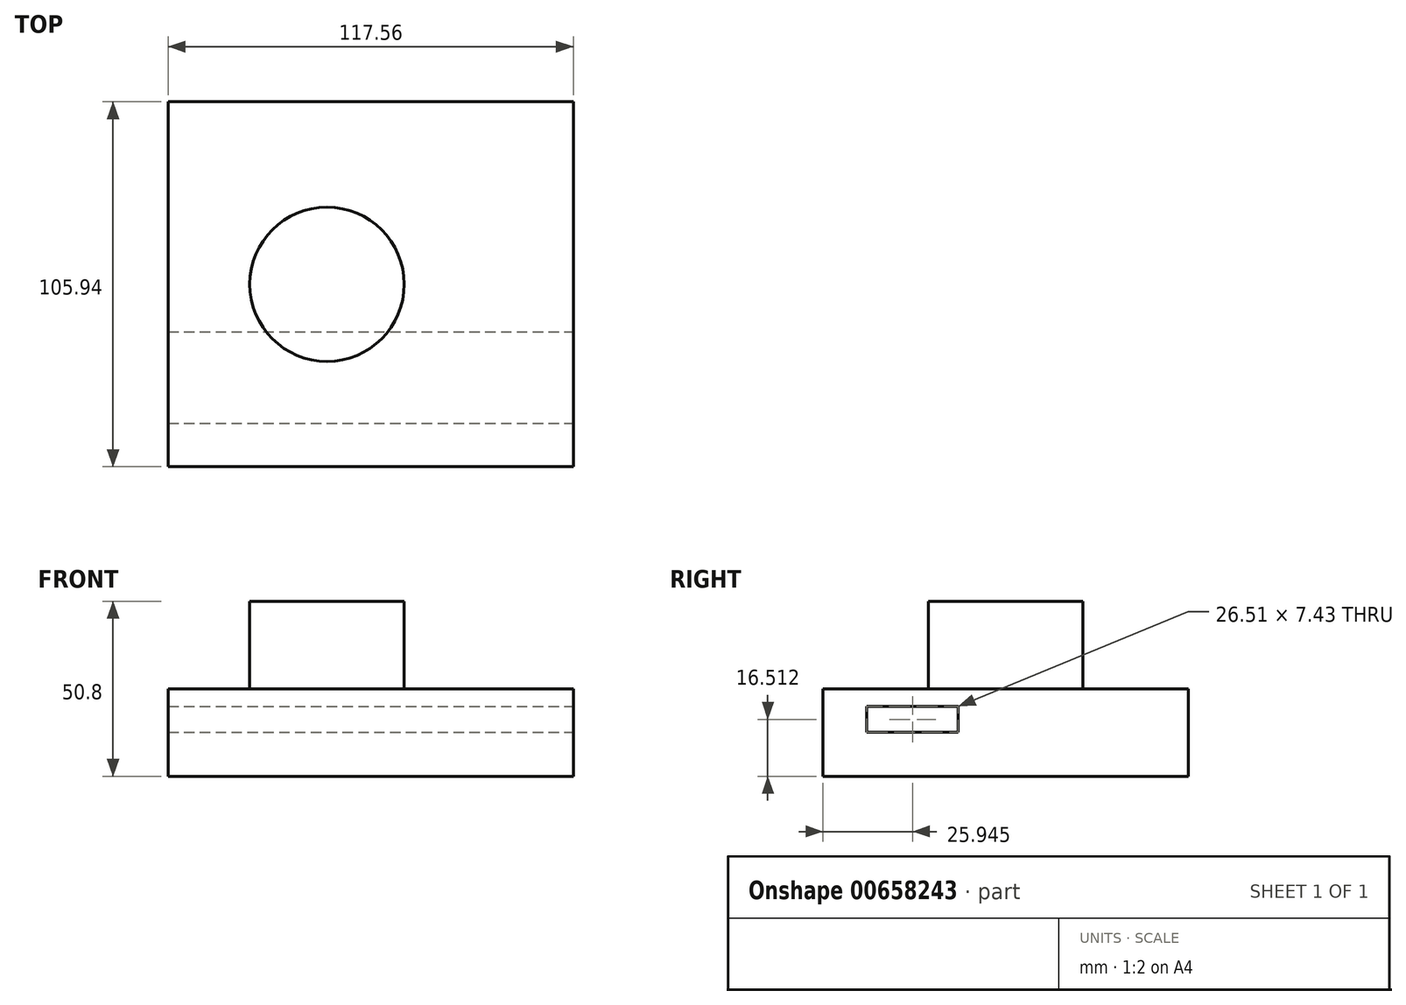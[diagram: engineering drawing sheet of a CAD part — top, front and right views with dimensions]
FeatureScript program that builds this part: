
annotation { "Feature Type Name" : "Feature", "Feature Type Description" : "" }
export const myFeature = defineFeature(function(context is Context, id is Id, definition is map)
    precondition{}
    {
        {
            var Q0;
            Q0=qCreatedBy(makeId("Top.planeOp"),FACE);
            var sketch = newSketch(context, id + "F0", { "sketchPlane" : qUnion([Q0])});
            skLineSegment(sketch, "E0.bottom", {"start": v(46.08, 52.97) * mm, "end": v(-46.08, 52.97) * mm});
            skLineSegment(sketch, "E0.top", {"start": v(46.08, -52.97) * mm, "end": v(-46.08, -52.97) * mm});
            skLineSegment(sketch, "E0.left", {"start": v(46.08, 52.97) * mm, "end": v(46.08, -52.97) * mm});
            skLineSegment(sketch, "E0.right", {"start": v(-46.08, 52.97) * mm, "end": v(-46.08, -52.97) * mm});
            skPoint(sketch, "E0.middle", {"position": v(0, 0) * mm});
            skSolve(sketch);
        }
        {
            var Q0;
            Q0 = qSketchRegion(id + "F0", true);
            extrude(context, id + "F1", {"entities" : qUnion([Q0]), "depth" : 25.4 * mm, "offsetDistance" : 25.4 * mm});
        }
        {
            var Q0;
            Q0=makeQuery(id+"F1.opExtrude","CAP_FACE",FACE,{"disambiguationData":[OSD([sQuery(id+"F0.wireOp",EDGE,"E0.bottom"),sQuery(id+"F0.wireOp",EDGE,"E0.top"),sQuery(id+"F0.wireOp",EDGE,"E0.left"),sQuery(id+"F0.wireOp",EDGE,"E0.right")])],"isStart":false});
            var sketch = newSketch(context, id + "F2", { "sketchPlane" : qUnion([Q0])});
            skCircle(sketch, "E1", {"center": v(0, 0) * mm, "radius": 22.4 * mm});
            skSolve(sketch);
        }
        {
            var Q0;
            Q0 = qSketchRegion(id + "F2", true);
            extrude(context, id + "F3", {"entities" : qUnion([Q0]), "operationType" : NewBodyOperationType.ADD, "depth" : 25.4 * mm, "offsetDistance" : 25.4 * mm});
        }
        {
            var Q0;
            Q0=makeQuery(id+"F1.opExtrude","SWEPT_FACE",FACE,{"disambiguationData":[OSD([sQuery(id+"F0.wireOp",EDGE,"E0.left")])]});
            extrude(context, id + "F4", {"entities" : qUnion([Q0]), "operationType" : NewBodyOperationType.ADD, "depth" : 25.4 * mm, "offsetDistance" : 25.4 * mm});
        }
        {
            var Q0;
            Q0=makeQuery(id+"F4.opExtrude","CAP_FACE",FACE,{"disambiguationData":[OSD([sQuery(id+"F0.wireOp",EDGE,"E0.left")])],"isStart":false});
            var sketch = newSketch(context, id + "F5", { "sketchPlane" : qUnion([Q0])});
            skLineSegment(sketch, "E2.bottom", {"start": v(-13.77, 12.8) * mm, "end": v(-40.28, 12.8) * mm});
            skLineSegment(sketch, "E2.top", {"start": v(-13.77, 20.23) * mm, "end": v(-40.28, 20.23) * mm});
            skLineSegment(sketch, "E2.left", {"start": v(-13.77, 12.8) * mm, "end": v(-13.77, 20.23) * mm});
            skLineSegment(sketch, "E2.right", {"start": v(-40.28, 12.8) * mm, "end": v(-40.28, 20.23) * mm});
            skPoint(sketch, "E2.middle", {"position": v(-27.03, 16.51) * mm});
            skSolve(sketch);
        }
        {
            var Q0;
            Q0 = qSketchRegion(id + "F5", true);
            extrude(context, id + "F6", {"entities" : qUnion([Q0]), "operationType" : NewBodyOperationType.REMOVE, "endBound" : BoundingType.THROUGH_ALL, "oppositeDirection" : true, "depth" : 25.4 * mm, "offsetDistance" : 25.4 * mm});
        }
    });
